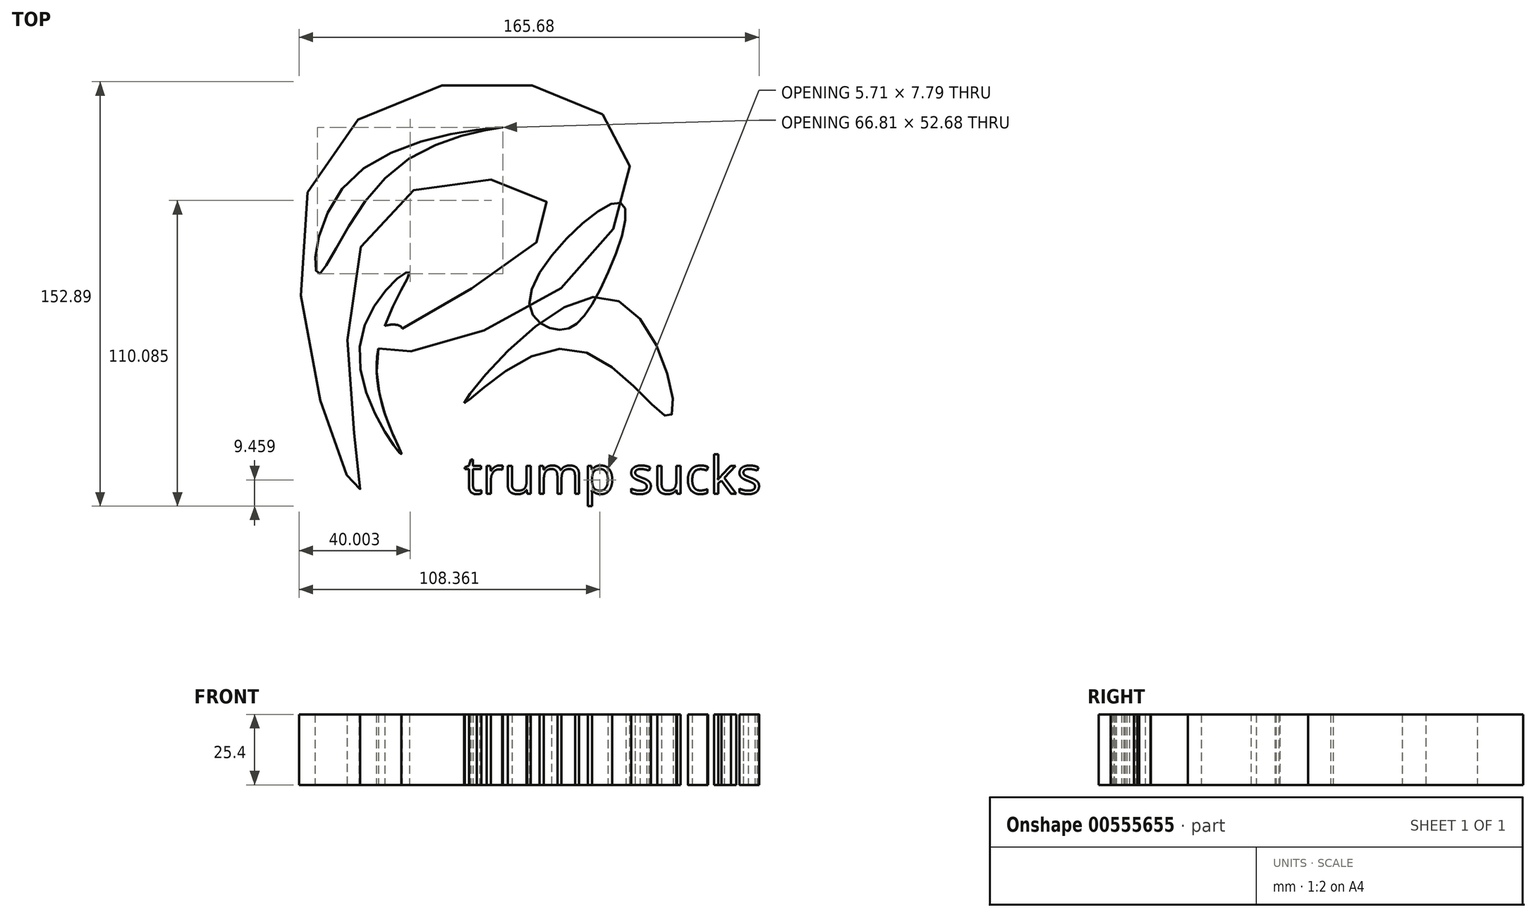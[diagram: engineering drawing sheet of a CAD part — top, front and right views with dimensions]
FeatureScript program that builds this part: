
annotation { "Feature Type Name" : "Feature", "Feature Type Description" : "" }
export const myFeature = defineFeature(function(context is Context, id is Id, definition is map)
    precondition{}
    {
        {
            var Q0;
            Q0=qCreatedBy(makeId("Top.planeOp"),FACE);
            var sketch = newSketch(context, id + "F0", { "sketchPlane" : qUnion([Q0])});
            skFitSpline(sketch, "E0", {"points": [v(31.66, 29.32) * mm, v(-30.65, -17.61) * mm, v(30.32, 0) * mm, v(52.17, 63.87) * mm, v(-52.61, 47.44) * mm, v(-37.9, -70.45) * mm, v(-30.45, 29.85) * mm, v(31.66, 29.32) * mm]});
            skFitSpline(sketch, "E1", {"points": [v(13.98, 61.22) * mm, v(-39.8, 43.59) * mm, v(-52.61, 8.43) * mm, v(-23.4, 47.44) * mm, v(13.98, 61.22) * mm]});
            skSolve(sketch);
        }
        {
            var Q0;
            Q0=makeQuery(id+"F0.imprint","IMPRINT",FACE,{"disambiguationData":[TD([[makeQuery(id+"F0.imprint","IMPRINT",EDGE,{"derivedFrom":sQuery(id+"F0.wireOp",EDGE,"E0")}),1.0]])]});
            extrude(context, id + "F1", {"entities" : qUnion([Q0]), "depth" : 25.4 * mm, "offsetDistance" : 25.4 * mm});
        }
        {
            var Q0;
            Q0=qCreatedBy(makeId("Top.planeOp"),FACE);
            var sketch = newSketch(context, id + "F2", { "sketchPlane" : qUnion([Q0])});
            skFitSpline(sketch, "E2", {"points": [v(-19.8, 9.22) * mm, v(-37.67, -17.94) * mm, v(-22.7, -56.42) * mm, v(-31.53, -23.55) * mm, v(-19.8, 9.22) * mm]});
            skSolve(sketch);
        }
        {
            var Q0;
            Q0 = qSketchRegion(id + "F2", true);
            extrude(context, id + "F3", {"entities" : qUnion([Q0]), "operationType" : NewBodyOperationType.ADD, "depth" : 25.4 * mm, "offsetDistance" : 25.4 * mm});
        }
        {
            var Q0;
            Q0=qCreatedBy(makeId("Top.planeOp"),FACE);
            var sketch = newSketch(context, id + "F4", { "sketchPlane" : qUnion([Q0])});
            skFitSpline(sketch, "E3", {"points": [v(0, -38.08) * mm, v(51.75, 0) * mm, v(74.42, -42.76) * mm, v(37.62, -18.47) * mm, v(0, -38.08) * mm]});
            skSolve(sketch);
        }
        {
            var Q0;
            Q0 = qSketchRegion(id + "F4", true);
            extrude(context, id + "F5", {"entities" : qUnion([Q0]), "depth" : 25.4 * mm, "offsetDistance" : 25.4 * mm});
        }
        {
            var Q0;
            Q0=qCreatedBy(makeId("Top.planeOp"),FACE);
            var sketch = newSketch(context, id + "F6", { "sketchPlane" : qUnion([Q0])});
            skFitSpline(sketch, "E4", {"points": [v(56.4, 34.02) * mm, v(47.53, 0) * mm, v(34.02, -11.67) * mm, v(23.6, 0) * mm, v(56.4, 34.02) * mm]});
            skSolve(sketch);
        }
        {
            var Q0;
            Q0 = qSketchRegion(id + "F6", true);
            extrude(context, id + "F7", {"entities" : qUnion([Q0]), "depth" : 25.4 * mm, "offsetDistance" : 25.4 * mm});
        }
        {
            var Q0;
            Q0=qCreatedBy(makeId("Top.planeOp"),FACE);
            var sketch = newSketch(context, id + "F8", { "sketchPlane" : qUnion([Q0])});
            skFitSpline(sketch, "E5", {"points": [v(-22.37, -11.45) * mm, v(-30.81, -11.34) * mm, v(-33.33, -18.27) * mm, v(-22.37, -11.45) * mm]});
            skSolve(sketch);
        }
        {
            var Q0;
            Q0 = qSketchRegion(id + "F8", true);
            extrude(context, id + "F9", {"entities" : qUnion([Q0]), "operationType" : NewBodyOperationType.ADD, "depth" : 25.4 * mm, "offsetDistance" : 25.4 * mm});
        }
        {
            var Q0;
            Q0=qCreatedBy(makeId("Top.planeOp"),FACE);
            var sketch = newSketch(context, id + "F10", { "sketchPlane" : qUnion([Q0])});
            skText(sketch, "E6", { "text": "trump sucks", "fontName": "OpenSans-Regular.ttf"});
            const initialGuessF10  = {"E6": [0, -0.07072, 1, 0, 0.01342]};
            skSetInitialGuess(sketch, initialGuessF10);
            skSolve(sketch);
        }
        {
            var Q0;
            Q0 = qSketchRegion(id + "F10", true);
            extrude(context, id + "F11", {"entities" : qUnion([Q0]), "depth" : 25.4 * mm, "offsetDistance" : 25.4 * mm});
        }
    });
